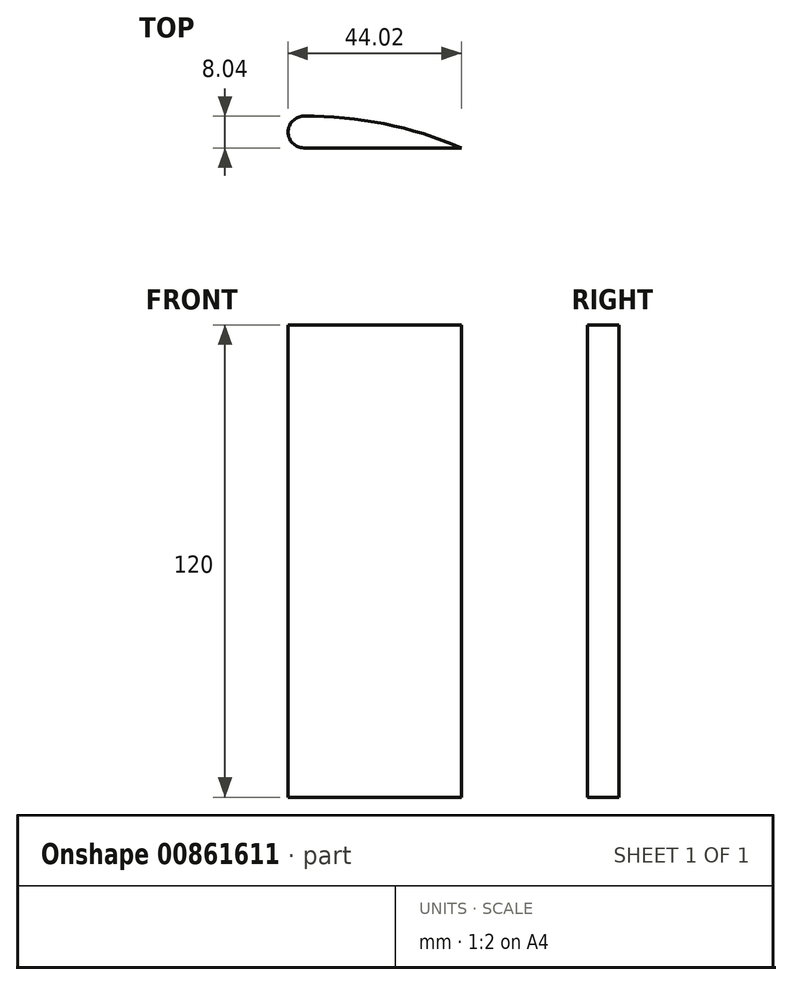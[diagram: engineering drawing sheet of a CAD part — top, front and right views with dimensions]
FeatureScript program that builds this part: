
annotation { "Feature Type Name" : "Feature", "Feature Type Description" : "" }
export const myFeature = defineFeature(function(context is Context, id is Id, definition is map)
    precondition{}
    {
        {
            var Q0;
            Q0=qCreatedBy(makeId("Top.planeOp"),FACE);
            var sketch = newSketch(context, id + "F0", { "sketchPlane" : qUnion([Q0])});
            skLineSegment(sketch, "E0", {"start": v(0, 0) * mm, "end": v(40, 0) * mm});
            skArc(sketch, "E1", {"start": v(0, 8.04) * mm, "mid": v(-4.02, 4.02) * mm, "end": v(0, 0) * mm});
            skArc(sketch, "E2", {"start": v(40, 0) * mm, "mid": v(20.42, 6.1) * mm, "end": v(0, 8.04) * mm});
            skSolve(sketch);
        }
        {
            var Q0;
            Q0 = qSketchRegion(id + "F0", true);
            extrude(context, id + "F1", {"entities" : qUnion([Q0]), "depth" : 120 * mm, "offsetDistance" : 25 * mm});
        }
    });
